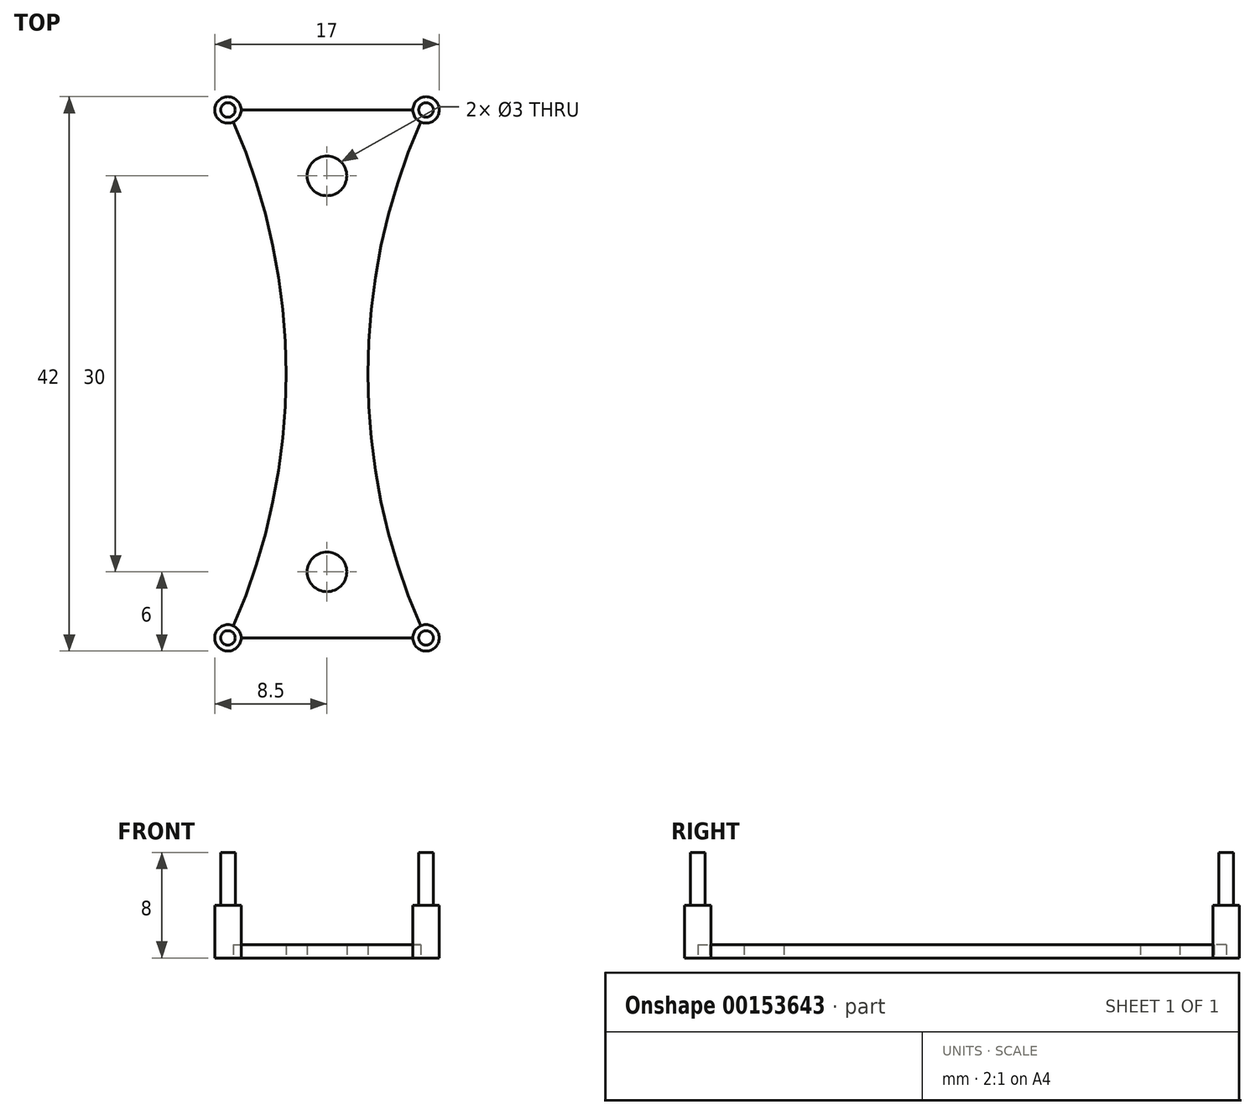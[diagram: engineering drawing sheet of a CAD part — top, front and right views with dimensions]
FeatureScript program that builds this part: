
annotation { "Feature Type Name" : "Feature", "Feature Type Description" : "" }
export const myFeature = defineFeature(function(context is Context, id is Id, definition is map)
    precondition{}
    {
        {
            var Q0;
            Q0=qCreatedBy(makeId("Top.planeOp"),FACE);
            var sketch = newSketch(context, id + "F0", { "sketchPlane" : qUnion([Q0])});
            skLineSegment(sketch, "E0.bottom", {"start": v(6.5, -20) * mm, "end": v(-6.5, -20) * mm});
            skLineSegment(sketch, "E0.top", {"start": v(6.5, 20) * mm, "end": v(-6.5, 20) * mm});
            skPoint(sketch, "E0.middle", {"position": v(0, 0) * mm});
            skCircle(sketch, "E1", {"center": v(7.5, 20) * mm, "radius": 1 * mm});
            skCircle(sketch, "E2", {"center": v(-7.5, 20) * mm, "radius": 1 * mm});
            skCircle(sketch, "E3", {"center": v(-7.5, -20) * mm, "radius": 1 * mm});
            skArc(sketch, "E4", {"start": v(-7.09, -19.09) * mm, "mid": v(-3.1, 0) * mm, "end": v(-7.09, 19.09) * mm});
            skArc(sketch, "E5", {"start": v(7.09, 19.09) * mm, "mid": v(3.1, 0) * mm, "end": v(7.09, -19.09) * mm});
            skCircle(sketch, "E6", {"center": v(7.5, -20) * mm, "radius": 1 * mm});
            skLineSegment(sketch, "E7", {"start": v(0, 0) * mm, "end": v(0, 15) * mm});
            skPoint(sketch, "E8.endSnap0", {"position": v(0, 7.5) * mm});
            skLineSegment(sketch, "E9", {"start": v(0, 0) * mm, "end": v(0, -15) * mm});
            skCircle(sketch, "E10", {"center": v(0, 15) * mm, "radius": 1.5 * mm});
            skCircle(sketch, "E11", {"center": v(0, -15) * mm, "radius": 1.5 * mm});
            skSolve(sketch);
        }
        {
            var Q0;
            {var subQ5=sQuery(id+"F0.wireOp",EDGE,"E0.bottom");Q0=makeQuery(id+"F0.imprint","IMPRINT",FACE,{"disambiguationData":[TD([[makeQuery(id+"F0.imprint","IMPRINT",EDGE,{"derivedFrom":subQ5}),-1.0]])]});}
            extrude(context, id + "F1", {"entities" : qUnion([Q0]), "depth" : 1 * mm});
        }
        {
            var Q0;
            {var subQ0=sQuery(id+"F0.wireOp",EDGE,"E1");var subQ1=makeQuery(id+"F0.imprint","INTERSECT",VERTEX,{"derivedFrom":[sQuery(id+"F0.wireOp",EDGE,"E0.top"),subQ0]});Q0=makeQuery(id+"F0.imprint","IMPRINT",FACE,{"disambiguationData":[TD([[makeQuery(id+"F0.imprint","IMPRINT",EDGE,{"disambiguationData":[TD([[subQ1,-1.0]])],"derivedFrom":subQ0}),1.0]])]});}
            extrude(context, id + "F2", {"entities" : qUnion([Q0]), "operationType" : NewBodyOperationType.ADD, "depth" : 4 * mm});
        }
        {
            var Q0;
            {var subQ0=sQuery(id+"F0.wireOp",EDGE,"E2");var subQ1=makeQuery(id+"F0.imprint","INTERSECT",VERTEX,{"derivedFrom":[sQuery(id+"F0.wireOp",EDGE,"E0.top"),subQ0]});Q0=makeQuery(id+"F0.imprint","IMPRINT",FACE,{"disambiguationData":[TD([[makeQuery(id+"F0.imprint","IMPRINT",EDGE,{"disambiguationData":[TD([[subQ1,-1.0]])],"derivedFrom":subQ0}),1.0]])]});}
            var Q1;
            {var subQ0=sQuery(id+"F0.wireOp",EDGE,"E6");var subQ1=makeQuery(id+"F0.imprint","INTERSECT",VERTEX,{"derivedFrom":[sQuery(id+"F0.wireOp",EDGE,"E0.bottom"),subQ0]});Q1=makeQuery(id+"F0.imprint","IMPRINT",FACE,{"disambiguationData":[TD([[makeQuery(id+"F0.imprint","IMPRINT",EDGE,{"disambiguationData":[TD([[subQ1,1.0]])],"derivedFrom":subQ0}),1.0]])]});}
            var Q2;
            {var subQ0=sQuery(id+"F0.wireOp",EDGE,"E3");var subQ1=makeQuery(id+"F0.imprint","INTERSECT",VERTEX,{"derivedFrom":[sQuery(id+"F0.wireOp",EDGE,"E0.bottom"),subQ0]});Q2=makeQuery(id+"F0.imprint","IMPRINT",FACE,{"disambiguationData":[TD([[makeQuery(id+"F0.imprint","IMPRINT",EDGE,{"disambiguationData":[TD([[subQ1,-1.0]])],"derivedFrom":subQ0}),1.0]])]});}
            extrude(context, id + "F3", {"entities" : qUnion([Q0, Q1, Q2]), "operationType" : NewBodyOperationType.ADD, "depth" : 4 * mm});
        }
        {
            var Q0;
            Q0=makeQuery(id+"F2.opExtrude","CAP_FACE",FACE,{"disambiguationData":[OSD([sQuery(id+"F0.wireOp",EDGE,"E1")])],"isStart":false});
            var sketch = newSketch(context, id + "F4", { "sketchPlane" : qUnion([Q0])});
            skCircle(sketch, "E12", {"center": v(7.5, 20) * mm, "radius": 0.55 * mm});
            skSolve(sketch);
        }
        {
            var Q0;
            Q0=makeQuery(id+"F4.imprint","IMPRINT",FACE,{"disambiguationData":[TD([[makeQuery(id+"F4.imprint","IMPRINT",EDGE,{"derivedFrom":sQuery(id+"F4.wireOp",EDGE,"E12")}),1.0]])]});
            extrude(context, id + "F5", {"entities" : qUnion([Q0]), "operationType" : NewBodyOperationType.ADD, "depth" : 4 * mm});
        }
        {
            var Q0;
            Q0=makeQuery(id+"F3.opExtrude","CAP_FACE",FACE,{"disambiguationData":[OSD([sQuery(id+"F0.wireOp",EDGE,"E2")])],"isStart":false});
            var sketch = newSketch(context, id + "F6", { "sketchPlane" : qUnion([Q0])});
            skCircle(sketch, "E13", {"center": v(-7.5, 20) * mm, "radius": 0.55 * mm});
            skSolve(sketch);
        }
        {
            var Q0;
            Q0=makeQuery(id+"F6.imprint","IMPRINT",FACE,{"disambiguationData":[TD([[makeQuery(id+"F6.imprint","IMPRINT",EDGE,{"derivedFrom":sQuery(id+"F6.wireOp",EDGE,"E13")}),1.0]])]});
            extrude(context, id + "F7", {"entities" : qUnion([Q0]), "operationType" : NewBodyOperationType.ADD, "depth" : 4 * mm});
        }
        {
            var Q0;
            Q0=makeQuery(id+"F3.opExtrude","CAP_FACE",FACE,{"disambiguationData":[OSD([sQuery(id+"F0.wireOp",EDGE,"E6")])],"isStart":false});
            var sketch = newSketch(context, id + "F8", { "sketchPlane" : qUnion([Q0])});
            skCircle(sketch, "E14", {"center": v(7.5, -20) * mm, "radius": 0.55 * mm});
            skSolve(sketch);
        }
        {
            var Q0;
            Q0 = qSketchRegion(id + "F8", true);
            extrude(context, id + "F9", {"entities" : qUnion([Q0]), "operationType" : NewBodyOperationType.ADD, "depth" : 4 * mm});
        }
        {
            var Q0;
            Q0=makeQuery(id+"F3.opExtrude","CAP_FACE",FACE,{"disambiguationData":[OSD([sQuery(id+"F0.wireOp",EDGE,"E3")])],"isStart":false});
            var sketch = newSketch(context, id + "F10", { "sketchPlane" : qUnion([Q0])});
            skCircle(sketch, "E15", {"center": v(-7.5, -20) * mm, "radius": 0.55 * mm});
            skSolve(sketch);
        }
        {
            var Q0;
            Q0 = qSketchRegion(id + "F10", true);
            extrude(context, id + "F11", {"entities" : qUnion([Q0]), "operationType" : NewBodyOperationType.ADD, "depth" : 4 * mm});
        }
    });
